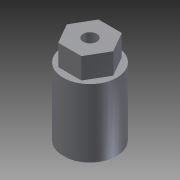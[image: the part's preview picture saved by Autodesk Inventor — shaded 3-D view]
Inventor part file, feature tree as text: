
AUTODESK INVENTOR PART (.ipt)
format: ipt  version: 2012 (Build 160160000, 160)  size: 123,392 bytes
history: native  units: mm
features: extrude x5, sketch x5, chamfer x2, projected_geometry x2
ambient origin geometry x8: Origin, YZ Plane, XZ Plane, XY Plane, X Axis, Y Axis, Z Axis, Center Point
bodies: Solid1 (feature_tree)
feature tree (14):
  extrude  "Extrusion1"  Depth=20.65mm TaperAngle=0.0deg
  chamfer  "Chamfer1"  Distance=0.5mm Angle=45.0deg
  extrude  "Extrusion2"  Depth=12.0mm
  extrude  "Extrusion3"  Depth=6.3mm TaperAngle=0.0deg
  extrude  "Extrusion4"  Depth=20.0mm TaperAngle=0.0deg
  chamfer  "Chamfer3"  Distance=0.5mm Angle=45.0deg
  extrude  "Extrusion5"  Depth=6.5mm
  sketch  "Sketch1"  dims[d0=16.0mm d1=20.65mm d2=0.0mm d3=0.5mm d4=2.0mm d5=45.0deg]
  sketch  "Sketch2"  dims[d7=6.3mm d8=0.0mm d9=12.0mm]
  projected_geometry  "Projected Loop1"
  sketch  "Sketch3"  dims[d10=4.1mm d11=6.3mm d12=0.0mm]
  sketch  "Sketch4"  dims[d16=6.2mm d17=20.0mm d18=0.0mm d19=0.5mm d20=2.0mm d21=45.0deg]
  sketch  "Sketch5"  dims[d22=4.8mm d23=6.5mm d24=10.0mm d25=0.0mm]
  projected_geometry  "Projected Loop2"
